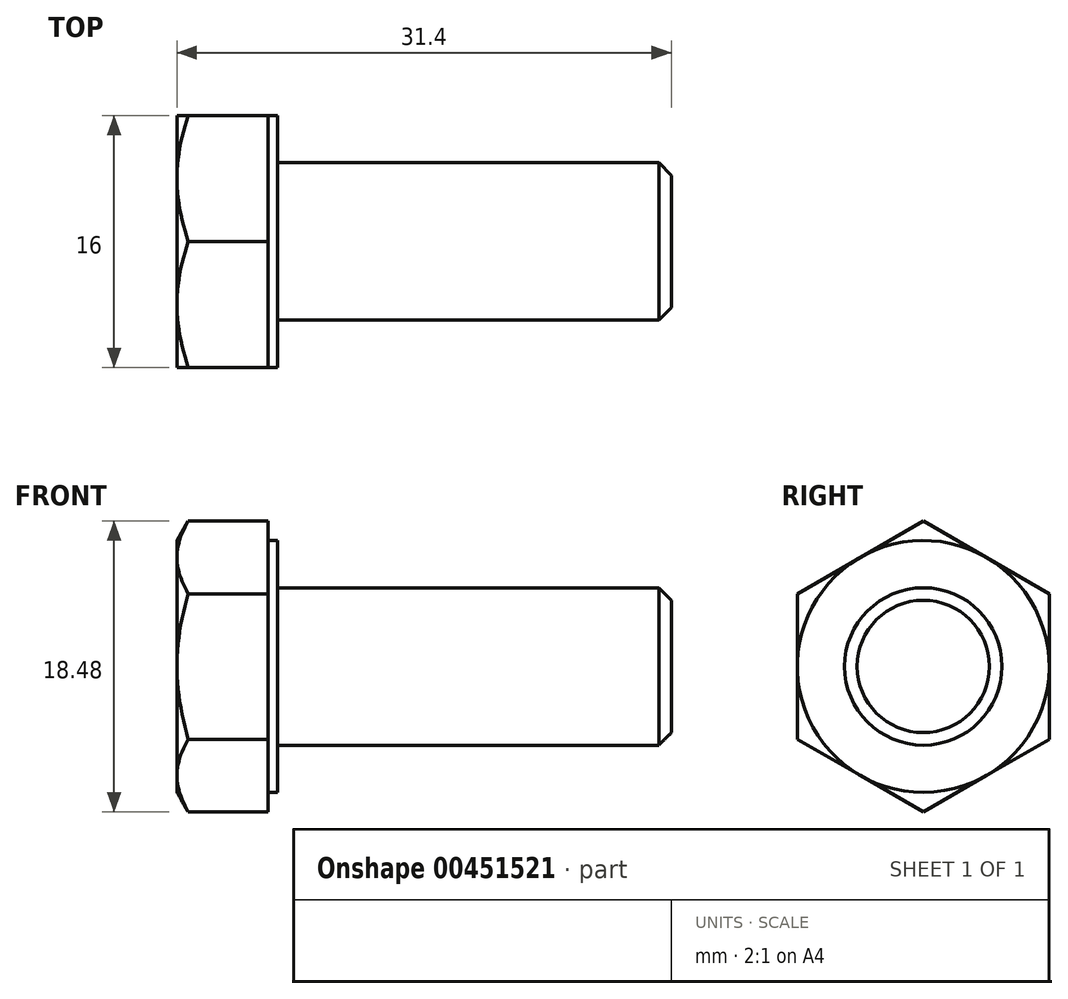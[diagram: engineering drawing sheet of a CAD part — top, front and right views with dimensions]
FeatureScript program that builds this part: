
annotation { "Feature Type Name" : "Feature", "Feature Type Description" : "" }
export const myFeature = defineFeature(function(context is Context, id is Id, definition is map)
    precondition{}
    {
        {
            var Q0;
            Q0=qCreatedBy(makeId("Right.planeOp"),FACE);
            var sketch = newSketch(context, id + "F0", { "sketchPlane" : qUnion([Q0])});
            skCircle(sketch, "E0.cCircle", {"center": v(0, 0) * mm, "radius": 8 * mm, "construction": true});
            skLineSegment(sketch, "E0.0", {"start": v(8, 4.62) * mm, "end": v(8, -4.62) * mm});
            skLineSegment(sketch, "E0.1", {"start": v(8, -4.62) * mm, "end": v(0, -9.24) * mm});
            skLineSegment(sketch, "E0.2", {"start": v(0, -9.24) * mm, "end": v(-8, -4.62) * mm});
            skLineSegment(sketch, "E0.3", {"start": v(-8, -4.62) * mm, "end": v(-8, 4.62) * mm});
            skLineSegment(sketch, "E0.4", {"start": v(-8, 4.62) * mm, "end": v(0, 9.24) * mm});
            skLineSegment(sketch, "E0.5", {"start": v(0, 9.24) * mm, "end": v(8, 4.62) * mm});
            skPoint(sketch, "E0.0.midPoint", {"position": v(8, 0) * mm});
            skSolve(sketch);
        }
        {
            var Q0;
            Q0=qSketchRegion(id+"F0",true);
            extrude(context, id + "F1", {"entities" : qUnion([Q0]), "depth" : 5.8 * mm});
        }
        {
            var Q0;
            Q0=makeQuery(id+"F1.opExtrude","CAP_FACE",FACE,{"disambiguationData":[OSD([sQuery(id+"F0.wireOp",EDGE,"E0.0"),sQuery(id+"F0.wireOp",EDGE,"E0.1"),sQuery(id+"F0.wireOp",EDGE,"E0.2"),sQuery(id+"F0.wireOp",EDGE,"E0.3"),sQuery(id+"F0.wireOp",EDGE,"E0.4"),sQuery(id+"F0.wireOp",EDGE,"E0.5")])],"isStart":false});
            var sketch = newSketch(context, id + "F2", { "sketchPlane" : qUnion([Q0])});
            skCircle(sketch, "E1", {"center": v(0, 0) * mm, "radius": 8 * mm});
            skSolve(sketch);
        }
        {
            var Q0;
            Q0=makeQuery(id+"F2.imprint","IMPRINT",FACE,{"disambiguationData":[TD([[makeQuery(id+"F2.imprint","IMPRINT",EDGE,{"derivedFrom":sQuery(id+"F2.wireOp",EDGE,"E1")}),1.0]])]});
            extrude(context, id + "F3", {"entities" : qUnion([Q0]), "operationType" : NewBodyOperationType.ADD, "depth" : 0.6 * mm});
        }
        {
            var Q0;
            Q0=makeQuery(id+"F3.opExtrude","CAP_FACE",FACE,{"disambiguationData":[OSD([sQuery(id+"F2.wireOp",EDGE,"E1")])],"isStart":false});
            var sketch = newSketch(context, id + "F4", { "sketchPlane" : qUnion([Q0])});
            skCircle(sketch, "E2", {"center": v(0, 0) * mm, "radius": 5 * mm});
            skSolve(sketch);
        }
        {
            var Q0;
            Q0=qSketchRegion(id+"F4",true);
            extrude(context, id + "F5", {"entities" : qUnion([Q0]), "operationType" : NewBodyOperationType.ADD, "depth" : 25 * mm});
        }
        {
            var Q0;
            Q0=makeQuery(id+"F5.opExtrude","CAP_EDGE",EDGE,{"disambiguationData":[OSD([sQuery(id+"F4.wireOp",EDGE,"E2")])],"isStart":false});
            chamfer(context, id + "F6", {"entities" : qUnion([Q0]), "width" : 0.8 * mm, "tangentPropagation" : true});
        }
        {
            var Q0;
            Q0=qCreatedBy(makeId("Front.planeOp"),FACE);
            var sketch = newSketch(context, id + "F7", { "sketchPlane" : qUnion([Q0])});
            skLineSegment(sketch, "E3", {"start": v(0, 9.24) * mm, "end": v(0, 8) * mm});
            skLineSegment(sketch, "E4", {"start": v(0, 8) * mm, "end": v(0.7, 9.24) * mm});
            skLineSegment(sketch, "E5", {"start": v(0.71, 9.24) * mm, "end": v(0, 9.24) * mm});
            skLineSegment(sketch, "E6", {"start": v(0, 0) * mm, "end": v(53.48, 0) * mm, "construction": true});
            skSolve(sketch);
        }
        {
            var Q0;
            Q0=qSketchRegion(id+"F7",true);
            var Q1;
            Q1=sQuery(id+"F7.wireOp",EDGE,"E6");
            revolve(context, id + "F8", {"operationType" : NewBodyOperationType.REMOVE, "entities" : qUnion([Q0]), "axis" : qUnion([Q1]), "revolveType" : RevolveType.FULL, "oppositeDirection" : true});
        }
    });
